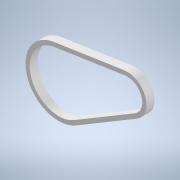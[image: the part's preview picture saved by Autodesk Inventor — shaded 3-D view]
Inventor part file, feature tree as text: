
AUTODESK INVENTOR PART (.ipt)
format: ipt  version: 2022.3 (Build 263350000, 350)  size: 128,512 bytes
history: native  units: mm
features: other x5, reference x4, sketch x1, plane x1, extrude x1, chamfer x1
ambient origin geometry x8: Origin, YZ Plane, XZ Plane, XY Plane, X Axis, Y Axis, Z Axis, Center Point
bodies: Solid1 (feature_tree)
feature tree (13):
  sketch  "Sketch1"  dims[d0=10.0mm d1=0.0mm d2=0.2mm d3=2.0mm d4=45.0deg]
  plane  "Work Plane1"
  extrude  "Extrusion1"  Depth=10.0mm TaperAngle=45.0deg
  chamfer  "Chamfer1"  [1 undecoded]
  reference  "Reference1"
  reference  "Reference2"
  reference  "Reference3"
  reference  "Reference4"
  other  "<userpath>\Documents\Inventor\NanoSumo\NanoSumo_part1.iam"
  other  "NanoSumo_part1.iam"
  other  "koło_pasowe_duze:1"
  other  "kółko:2"
  other  "silnik:1"
note: 1 required parameter value undecoded (feature->parameter linkage not recoverable at this tier; creation-order binding heuristic only, values carry confidence <= 0.55)
